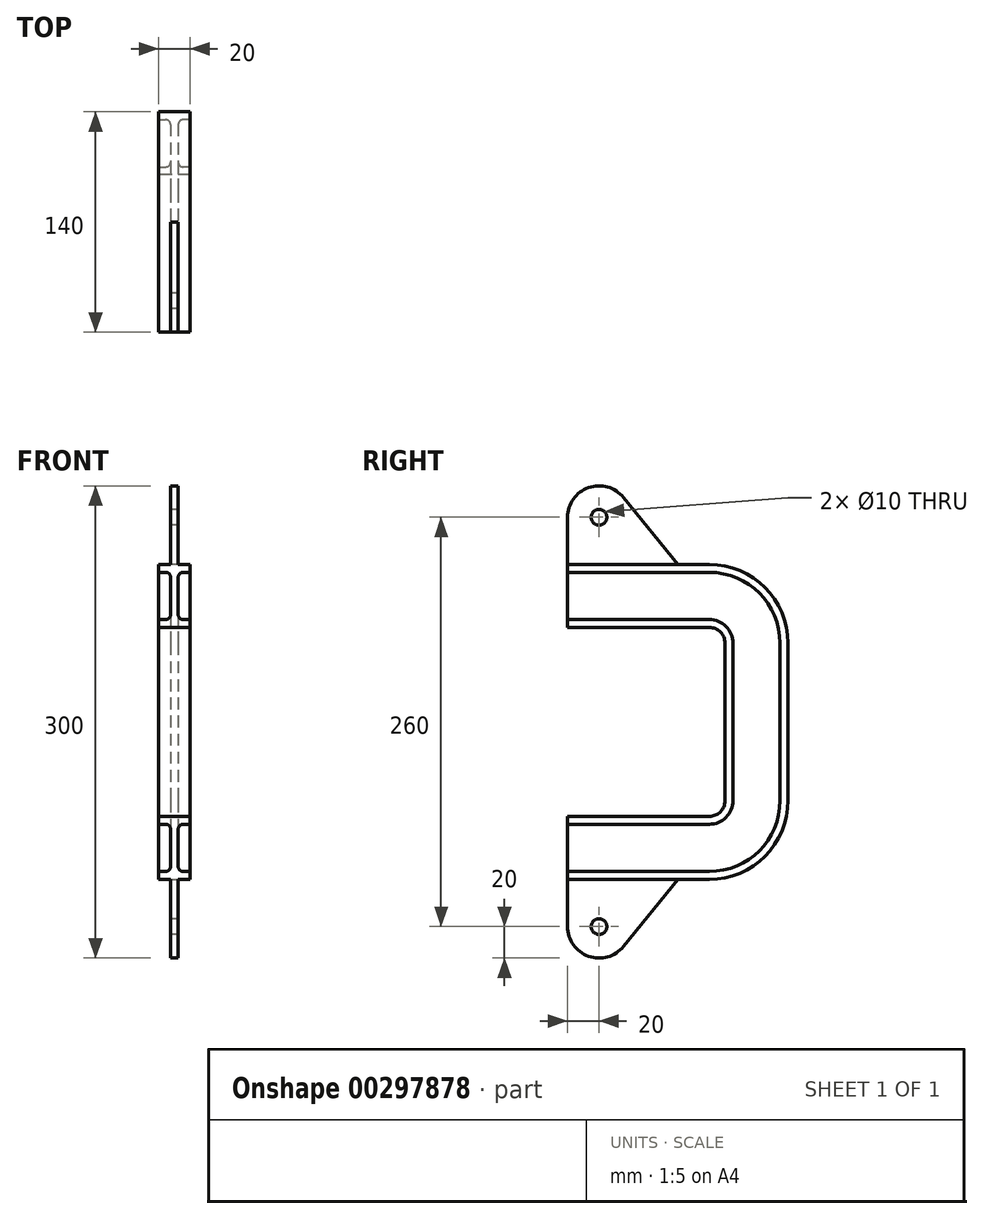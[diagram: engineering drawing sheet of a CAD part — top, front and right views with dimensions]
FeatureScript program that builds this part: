
annotation { "Feature Type Name" : "Feature", "Feature Type Description" : "" }
export const myFeature = defineFeature(function(context is Context, id is Id, definition is map)
    precondition{}
    {
        {
            var Q0;
            Q0=qCreatedBy(makeId("Front.planeOp"),FACE);
            var sketch = newSketch(context, id + "F0", { "sketchPlane" : qUnion([Q0])});
            skLineSegment(sketch, "E0", {"start": v(0, 20) * mm, "end": v(10, 20) * mm});
            skLineSegment(sketch, "E1", {"start": v(10, 20) * mm, "end": v(10, 15) * mm});
            skLineSegment(sketch, "E2", {"start": v(10, 15) * mm, "end": v(5.5, 15) * mm});
            skLineSegment(sketch, "E3", {"start": v(2.5, 12) * mm, "end": v(2.5, 0) * mm});
            skPoint(sketch, "E4.visualSharp", {"position": v(2.5, 15) * mm});
            skArc(sketch, "E4.filletArc", {"start": v(5.5, 15) * mm, "mid": v(3.38, 14.12) * mm, "end": v(2.5, 12) * mm});
            skArc(sketch, "E5.MirrorCS", {"start": v(-5.5, 15) * mm, "mid": v(-3.38, 14.12) * mm, "end": v(-2.5, 12) * mm});
            skLineSegment(sketch, "E6.MirrorCS", {"start": v(0, 20) * mm, "end": v(-10, 20) * mm});
            skLineSegment(sketch, "E7.MirrorCS", {"start": v(-10, 20) * mm, "end": v(-10, 15) * mm});
            skPoint(sketch, "E8.MirrorP", {"position": v(-2.5, 15) * mm});
            skLineSegment(sketch, "E9.MirrorCS", {"start": v(-10, 15) * mm, "end": v(-5.5, 15) * mm});
            skLineSegment(sketch, "E10.MirrorCS", {"start": v(-2.5, 12) * mm, "end": v(-2.5, 0) * mm});
            skArc(sketch, "E11.MirrorCS", {"start": v(-5.5, -15) * mm, "mid": v(-3.38, -14.12) * mm, "end": v(-2.5, -12) * mm});
            skArc(sketch, "E12.MirrorCS", {"start": v(5.5, -15) * mm, "mid": v(3.38, -14.12) * mm, "end": v(2.5, -12) * mm});
            skPoint(sketch, "E13.MirrorP", {"position": v(-2.5, -15) * mm});
            skLineSegment(sketch, "E14.MirrorCS", {"start": v(-2.5, -12) * mm, "end": v(-2.5, 0) * mm});
            skLineSegment(sketch, "E15.MirrorCS", {"start": v(-10, -15) * mm, "end": v(-5.5, -15) * mm});
            skLineSegment(sketch, "E16.MirrorCS", {"start": v(-10, -20) * mm, "end": v(-10, -15) * mm});
            skLineSegment(sketch, "E17.MirrorCS", {"start": v(0, -20) * mm, "end": v(-10, -20) * mm});
            skLineSegment(sketch, "E18.MirrorCS", {"start": v(10, -20) * mm, "end": v(10, -15) * mm});
            skLineSegment(sketch, "E19.MirrorCS", {"start": v(10, -15) * mm, "end": v(5.5, -15) * mm});
            skPoint(sketch, "E20.MirrorP", {"position": v(2.5, -15) * mm});
            skLineSegment(sketch, "E21.MirrorCS", {"start": v(0, -20) * mm, "end": v(10, -20) * mm});
            skLineSegment(sketch, "E22.MirrorCS", {"start": v(2.5, -12) * mm, "end": v(2.5, 0) * mm});
            skSolve(sketch);
        }
        {
            var Q0;
            Q0=qCreatedBy(makeId("Right.planeOp"),FACE);
            var sketch = newSketch(context, id + "F1", { "sketchPlane" : qUnion([Q0])});
            skLineSegment(sketch, "E23", {"start": v(0, -20) * mm, "end": v(90, -20) * mm});
            skLineSegment(sketch, "E24", {"start": v(100, -30) * mm, "end": v(100, -80) * mm});
            skPoint(sketch, "E25.visualSharp", {"position": v(100, -20) * mm});
            skArc(sketch, "E25.filletArc", {"start": v(100, -30) * mm, "mid": v(97.07, -22.93) * mm, "end": v(90, -20) * mm});
            skLineSegment(sketch, "E26", {"start": v(41.83, -80) * mm, "end": v(185.52, -80) * mm, "construction": true});
            skArc(sketch, "E27.MirrorCS", {"start": v(100, -130) * mm, "mid": v(97.07, -137.07) * mm, "end": v(90, -140) * mm});
            skLineSegment(sketch, "E28.MirrorCS", {"start": v(100, -130) * mm, "end": v(100, -80) * mm});
            skLineSegment(sketch, "E29.MirrorCS", {"start": v(0, -140) * mm, "end": v(90, -140) * mm});
            skPoint(sketch, "E30.MirrorP", {"position": v(100, -140) * mm});
            skSolve(sketch);
        }
        {
            var Q0;
            Q0=makeQuery(id+"F0.imprint","IMPRINT",FACE,{"disambiguationData":[TD([[makeQuery(id+"F0.imprint","IMPRINT",EDGE,{"derivedFrom":sQuery(id+"F0.wireOp",EDGE,"E0")}),-1.0]])]});
            var Q1;
            Q1=sQuery(id+"F1.wireOp",EDGE,"E23");
            var Q2;
            Q2=sQuery(id+"F1.wireOp",EDGE,"E25.filletArc");
            var Q3;
            Q3=sQuery(id+"F1.wireOp",EDGE,"E24");
            var Q4;
            Q4=sQuery(id+"F1.wireOp",EDGE,"E28.MirrorCS");
            var Q5;
            Q5=sQuery(id+"F1.wireOp",EDGE,"E27.MirrorCS");
            var Q6;
            Q6=sQuery(id+"F1.wireOp",EDGE,"E29.MirrorCS");
            sweep(context, id + "F2", {"profiles" : qUnion([Q0]), "path" : qUnion([Q1, Q2, Q3, Q4, Q5, Q6])});
        }
        {
            var Q0;
            Q0=qCreatedBy(makeId("Right.planeOp"),FACE);
            var sketch = newSketch(context, id + "F3", { "sketchPlane" : qUnion([Q0])});
            skLineSegment(sketch, "E31", {"start": v(0, 20) * mm, "end": v(70, 20) * mm});
            skLineSegment(sketch, "E32", {"start": v(70, 20) * mm, "end": v(35.55, 62.58) * mm});
            skArc(sketch, "E33", {"start": v(35.55, 62.58) * mm, "mid": v(13.33, 68.85) * mm, "end": v(0, 50) * mm});
            skLineSegment(sketch, "E34", {"start": v(0, 20) * mm, "end": v(0, 50) * mm});
            skCircle(sketch, "E35", {"center": v(20, 50) * mm, "radius": 5 * mm});
            skLineSegment(sketch, "E36", {"start": v(56.27, -80) * mm, "end": v(156.77, -80) * mm, "construction": true});
            skCircle(sketch, "E37.MirrorC", {"center": v(20, -210) * mm, "radius": 5 * mm});
            skLineSegment(sketch, "E38.MirrorCS", {"start": v(0, -180) * mm, "end": v(0, -210) * mm});
            skLineSegment(sketch, "E39.MirrorCS", {"start": v(0, -180) * mm, "end": v(70, -180) * mm});
            skArc(sketch, "E40.MirrorCS", {"start": v(35.55, -222.58) * mm, "mid": v(13.33, -228.85) * mm, "end": v(0, -210) * mm});
            skLineSegment(sketch, "E41.MirrorCS", {"start": v(70, -180) * mm, "end": v(35.55, -222.58) * mm});
            skSolve(sketch);
        }
        {
            var Q0;
            Q0 = qSketchRegion(id + "F3", true);
            extrude(context, id + "F4", {"entities" : qUnion([Q0]), "operationType" : NewBodyOperationType.ADD, "endBound" : BoundingType.SYMMETRIC, "depth" : 5 * mm});
        }
    });
